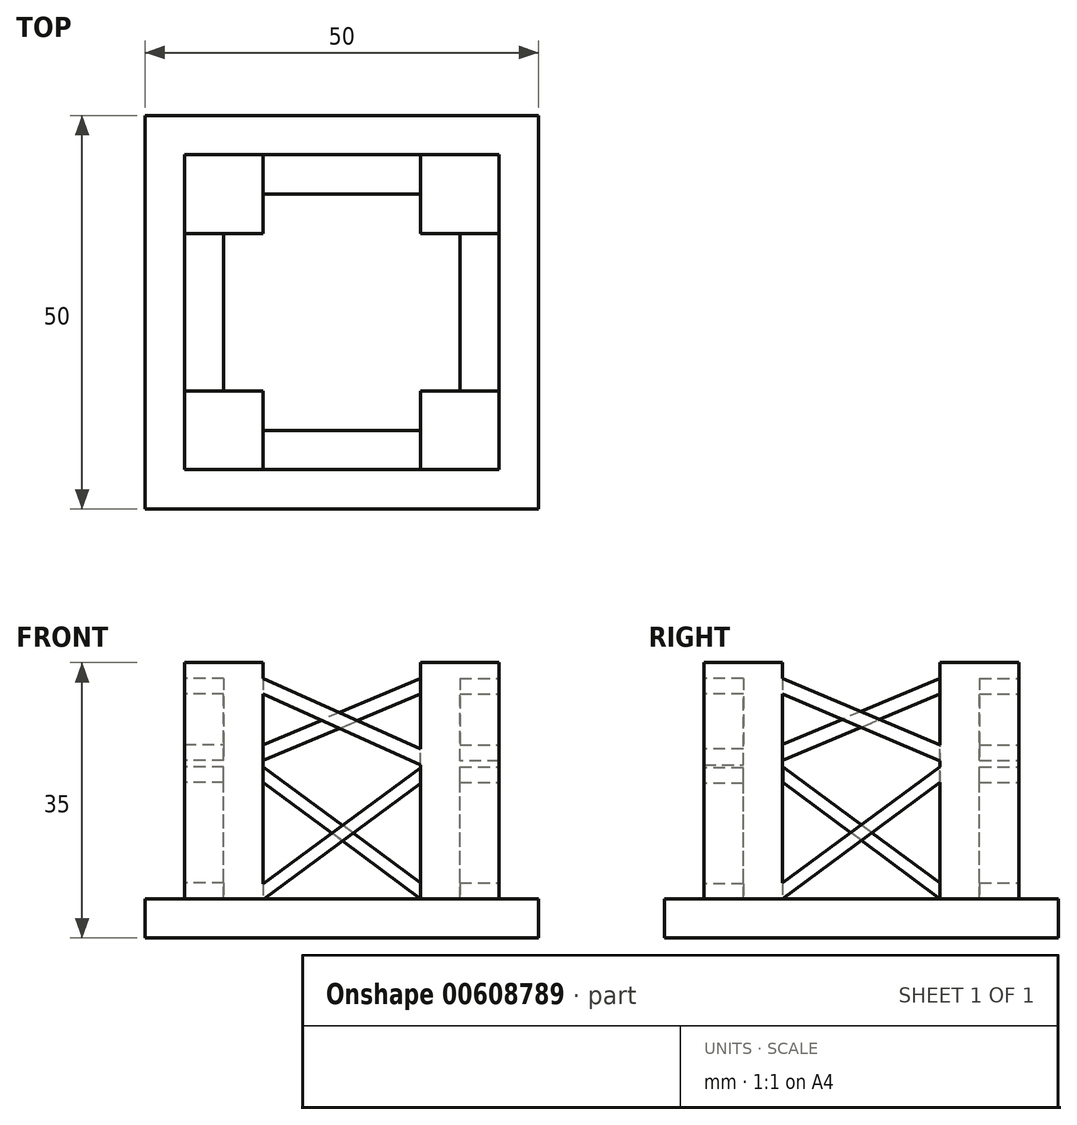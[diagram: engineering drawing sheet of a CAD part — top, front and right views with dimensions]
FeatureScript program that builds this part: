
annotation { "Feature Type Name" : "Feature", "Feature Type Description" : "" }
export const myFeature = defineFeature(function(context is Context, id is Id, definition is map)
    precondition{}
    {
        {
            var Q0;
            Q0=qCreatedBy(makeId("Top.planeOp"),FACE);
            var sketch = newSketch(context, id + "F0", { "sketchPlane" : qUnion([Q0])});
            skLineSegment(sketch, "E0.bottom", {"start": v(25, -25) * mm, "end": v(-25, -25) * mm});
            skLineSegment(sketch, "E0.top", {"start": v(25, 25) * mm, "end": v(-25, 25) * mm});
            skLineSegment(sketch, "E0.left", {"start": v(25, -25) * mm, "end": v(25, 25) * mm});
            skLineSegment(sketch, "E0.right", {"start": v(-25, -25) * mm, "end": v(-25, 25) * mm});
            skPoint(sketch, "E0.middle", {"position": v(0, 0) * mm});
            skSolve(sketch);
        }
        {
            var Q0;
            Q0 = qSketchRegion(id + "F0", true);
            extrude(context, id + "F1", {"entities" : qUnion([Q0]), "depth" : 5 * mm, "offsetDistance" : 25 * mm});
        }
        {
            var Q0;
            Q0=makeQuery(id+"F1.opExtrude","CAP_FACE",FACE,{"disambiguationData":[OSD([sQuery(id+"F0.wireOp",EDGE,"E0.bottom"),sQuery(id+"F0.wireOp",EDGE,"E0.top"),sQuery(id+"F0.wireOp",EDGE,"E0.left"),sQuery(id+"F0.wireOp",EDGE,"E0.right")])],"isStart":false});
            var sketch = newSketch(context, id + "F2", { "sketchPlane" : qUnion([Q0])});
            skLineSegment(sketch, "E1.bottom", {"start": v(-10, 10) * mm, "end": v(-20, 10) * mm});
            skLineSegment(sketch, "E1.top", {"start": v(-10, 20) * mm, "end": v(-20, 20) * mm});
            skLineSegment(sketch, "E1.left", {"start": v(-10, 10) * mm, "end": v(-10, 20) * mm});
            skLineSegment(sketch, "E1.right", {"start": v(-20, 10) * mm, "end": v(-20, 20) * mm});
            skPoint(sketch, "E1.middle", {"position": v(-15, 15) * mm});
            skPoint(sketch, "E2.0.1.0", {"position": v(-15, -15) * mm});
            skLineSegment(sketch, "E2.0.1.1", {"start": v(-10, -20) * mm, "end": v(-20, -20) * mm});
            skLineSegment(sketch, "E2.0.1.2", {"start": v(-10, -10) * mm, "end": v(-20, -10) * mm});
            skLineSegment(sketch, "E2.0.1.3", {"start": v(-10, -20) * mm, "end": v(-10, -10) * mm});
            skLineSegment(sketch, "E2.0.1.4", {"start": v(-20, -20) * mm, "end": v(-20, -10) * mm});
            skPoint(sketch, "E2.1.0.0", {"position": v(15, 15) * mm});
            skLineSegment(sketch, "E2.1.0.1", {"start": v(20, 10) * mm, "end": v(10, 10) * mm});
            skLineSegment(sketch, "E2.1.0.2", {"start": v(20, 20) * mm, "end": v(10, 20) * mm});
            skLineSegment(sketch, "E2.1.0.3", {"start": v(20, 10) * mm, "end": v(20, 20) * mm});
            skLineSegment(sketch, "E2.1.0.4", {"start": v(10, 10) * mm, "end": v(10, 20) * mm});
            skPoint(sketch, "E2.1.1.0", {"position": v(15, -15) * mm});
            skLineSegment(sketch, "E2.1.1.1", {"start": v(20, -20) * mm, "end": v(10, -20) * mm});
            skLineSegment(sketch, "E2.1.1.2", {"start": v(20, -10) * mm, "end": v(10, -10) * mm});
            skLineSegment(sketch, "E2.1.1.3", {"start": v(20, -20) * mm, "end": v(20, -10) * mm});
            skLineSegment(sketch, "E2.1.1.4", {"start": v(10, -20) * mm, "end": v(10, -10) * mm});
            skLineSegment(sketch, "E2.direction1", {"start": v(-20, 10) * mm, "end": v(10, 10) * mm, "construction": true});
            skLineSegment(sketch, "E2.direction2", {"start": v(-20, 10) * mm, "end": v(-20, -20) * mm, "construction": true});
            skSolve(sketch);
        }
        {
            var Q0;
            Q0 = qSketchRegion(id + "F2", true);
            extrude(context, id + "F3", {"entities" : qUnion([Q0]), "operationType" : NewBodyOperationType.ADD, "depth" : 30 * mm, "offsetDistance" : 25 * mm});
        }
        {
            var Q0;
            Q0=makeQuery(id+"F3.opExtrude","SWEPT_FACE",FACE,{"disambiguationData":[OSD([sQuery(id+"F2.wireOp",EDGE,"E2.0.1.1")])]});
            var sketch = newSketch(context, id + "F4", { "sketchPlane" : qUnion([Q0])});
            skLineSegment(sketch, "E3", {"start": v(-10, 4.9) * mm, "end": v(9.98, 19.64) * mm});
            skLineSegment(sketch, "E4", {"start": v(-10, 6.9) * mm, "end": v(9.98, 21.64) * mm});
            skLineSegment(sketch, "E5", {"start": v(9.98, 19.64) * mm, "end": v(9.98, 21.64) * mm});
            skLineSegment(sketch, "E6", {"start": v(10.1, 21.98) * mm, "end": v(-10, 31) * mm});
            skLineSegment(sketch, "E7", {"start": v(-10, 31) * mm, "end": v(-10, 33) * mm});
            skLineSegment(sketch, "E8", {"start": v(-10, 33) * mm, "end": v(10.1, 23.98) * mm});
            skLineSegment(sketch, "E9", {"start": v(10.1, 23.98) * mm, "end": v(10.1, 21.98) * mm});
            skLineSegment(sketch, "E10", {"start": v(-10, 6.9) * mm, "end": v(-10, 4.9) * mm});
            skSolve(sketch);
        }
        {
            var Q0;
            Q0=makeQuery(id+"F3.opExtrude","SWEPT_FACE",FACE,{"disambiguationData":[OSD([sQuery(id+"F2.wireOp",EDGE,"E2.1.1.3")])]});
            var sketch = newSketch(context, id + "F5", { "sketchPlane" : qUnion([Q0])});
            skLineSegment(sketch, "E11", {"start": v(-10, 5) * mm, "end": v(10.02, 19.78) * mm});
            skLineSegment(sketch, "E12", {"start": v(-10, 7) * mm, "end": v(10.02, 21.78) * mm});
            skLineSegment(sketch, "E13", {"start": v(10.02, 19.78) * mm, "end": v(10.02, 21.78) * mm});
            skLineSegment(sketch, "E14", {"start": v(10.02, 22.5) * mm, "end": v(-10, 31) * mm});
            skLineSegment(sketch, "E15", {"start": v(-10, 31) * mm, "end": v(-10, 33) * mm});
            skLineSegment(sketch, "E16", {"start": v(-10, 33) * mm, "end": v(10.02, 24.5) * mm});
            skLineSegment(sketch, "E17", {"start": v(10.02, 24.5) * mm, "end": v(10.02, 22.5) * mm});
            skSolve(sketch);
        }
        {
            var Q0;
            Q0 = qSketchRegion(id + "F5", true);
            var Q1;
            {var subQ0=sQuery(id+"F5.wireOp",EDGE,"E11");Q1=makeQuery(id+"F5.imprint","IMPRINT",FACE,{"disambiguationData":[TD([[makeQuery(id+"F5.imprint","IMPRINT",EDGE,{"derivedFrom":subQ0}),1.0]])]});}
            extrude(context, id + "F6", {"entities" : qUnion([Q0, Q1]), "operationType" : NewBodyOperationType.ADD, "oppositeDirection" : true, "depth" : 5 * mm, "offsetDistance" : 25 * mm});
        }
        {
            var Q0;
            Q0=makeQuery(id+"F3.opExtrude","SWEPT_FACE",FACE,{"disambiguationData":[OSD([sQuery(id+"F2.wireOp",EDGE,"E2.1.0.2")])]});
            var sketch = newSketch(context, id + "F7", { "sketchPlane" : qUnion([Q0])});
            skLineSegment(sketch, "E18", {"start": v(-10, 5) * mm, "end": v(9.98, 19.75) * mm});
            skLineSegment(sketch, "E19", {"start": v(-10, 7) * mm, "end": v(9.98, 21.75) * mm});
            skLineSegment(sketch, "E20", {"start": v(9.98, 19.75) * mm, "end": v(9.98, 21.75) * mm});
            skLineSegment(sketch, "E21", {"start": v(10, 22.54) * mm, "end": v(-10, 31) * mm});
            skLineSegment(sketch, "E22", {"start": v(-10, 31) * mm, "end": v(-10, 33) * mm});
            skLineSegment(sketch, "E23", {"start": v(-10, 33) * mm, "end": v(10, 24.54) * mm});
            skLineSegment(sketch, "E24", {"start": v(10, 24.54) * mm, "end": v(10, 22.54) * mm});
            skSolve(sketch);
        }
        {
            var Q0;
            Q0=makeQuery(id+"F7.imprint","IMPRINT",FACE,{"disambiguationData":[TD([[makeQuery(id+"F7.imprint","IMPRINT",EDGE,{"derivedFrom":sQuery(id+"F7.wireOp",EDGE,"E21")}),-1.0]])]});
            var Q1;
            {var subQ0=sQuery(id+"F7.wireOp",EDGE,"E18");Q1=makeQuery(id+"F7.imprint","IMPRINT",FACE,{"disambiguationData":[TD([[makeQuery(id+"F7.imprint","IMPRINT",EDGE,{"derivedFrom":subQ0}),1.0]])]});}
            extrude(context, id + "F8", {"entities" : qUnion([Q0, Q1]), "operationType" : NewBodyOperationType.ADD, "oppositeDirection" : true, "depth" : 5 * mm, "offsetDistance" : 25 * mm});
        }
        {
            var Q0;
            Q0=makeQuery(id+"F3.opExtrude","SWEPT_FACE",FACE,{"disambiguationData":[OSD([sQuery(id+"F2.wireOp",EDGE,"E1.right")])]});
            var sketch = newSketch(context, id + "F9", { "sketchPlane" : qUnion([Q0])});
            skLineSegment(sketch, "E25", {"start": v(-10, 5) * mm, "end": v(9.98, 19.75) * mm});
            skLineSegment(sketch, "E26", {"start": v(-10, 7) * mm, "end": v(9.98, 21.75) * mm});
            skLineSegment(sketch, "E27", {"start": v(9.98, 19.75) * mm, "end": v(9.98, 21.75) * mm});
            skLineSegment(sketch, "E28", {"start": v(10.1, 22.53) * mm, "end": v(-10, 31) * mm});
            skLineSegment(sketch, "E29", {"start": v(-10, 31) * mm, "end": v(-10, 33) * mm});
            skLineSegment(sketch, "E30", {"start": v(-10, 33) * mm, "end": v(10.1, 24.53) * mm});
            skLineSegment(sketch, "E31", {"start": v(10.1, 24.53) * mm, "end": v(10.1, 22.53) * mm});
            skSolve(sketch);
        }
        {
            var Q0;
            Q0=makeQuery(id+"F9.imprint","IMPRINT",FACE,{"disambiguationData":[TD([[makeQuery(id+"F9.imprint","IMPRINT",EDGE,{"derivedFrom":sQuery(id+"F9.wireOp",EDGE,"E28")}),-1.0]])]});
            var Q1;
            {var subQ0=sQuery(id+"F9.wireOp",EDGE,"E25");Q1=makeQuery(id+"F9.imprint","IMPRINT",FACE,{"disambiguationData":[TD([[makeQuery(id+"F9.imprint","IMPRINT",EDGE,{"derivedFrom":subQ0}),1.0]])]});}
            extrude(context, id + "F10", {"entities" : qUnion([Q0, Q1]), "operationType" : NewBodyOperationType.ADD, "oppositeDirection" : true, "depth" : 5 * mm, "offsetDistance" : 25 * mm});
        }
        {
            var Q0;
            Q0 = qSketchRegion(id + "F4", true);
            extrude(context, id + "F11", {"entities" : qUnion([Q0]), "operationType" : NewBodyOperationType.ADD, "oppositeDirection" : true, "depth" : 5 * mm, "offsetDistance" : 25 * mm});
        }
    });
